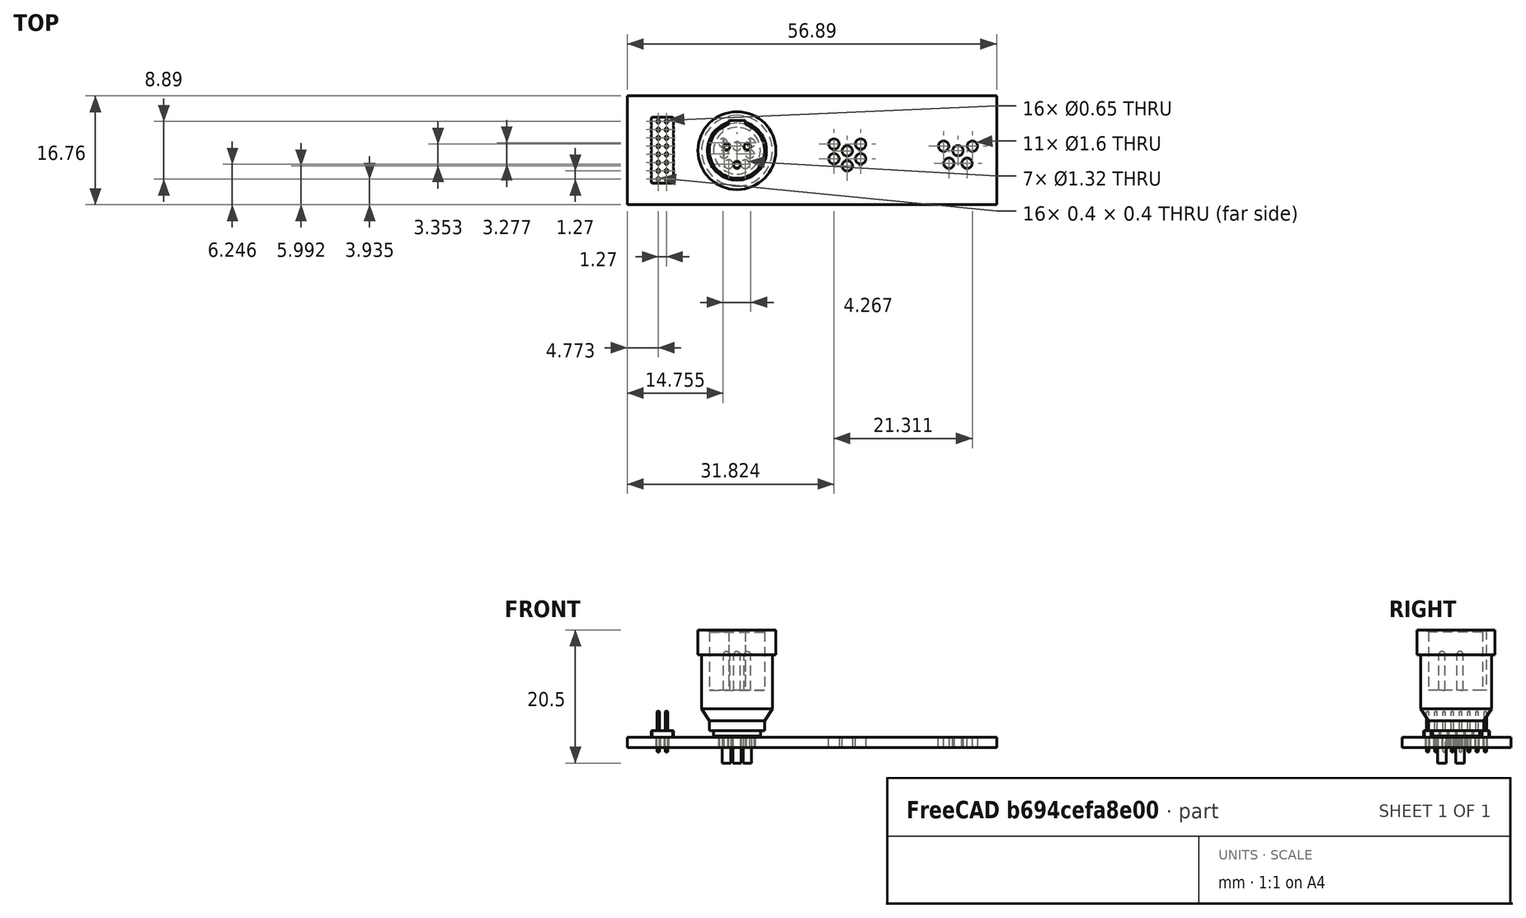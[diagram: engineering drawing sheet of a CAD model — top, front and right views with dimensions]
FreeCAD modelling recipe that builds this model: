
FCSTD DOCUMENT  (FreeCAD 1.0R39109 (Git))
Label: ConnectorInterfaceBoard
License: All rights reserved
LicenseURL: http://en.wikipedia.org/wiki/All_rights_reserved
objects: Part::Feature×9, App::Part×4, App::Link×2, PartDesign::CoordinateSystem×1, Sketcher::SketchObject×1
note: 12 computed .brp shape members not serialized (recipe doc carries the construction recipe); baked Part::Feature solids carry a one-line shape summary decoded from their .brp

FEATURE [PartDesign::CoordinateSystem] Local_CS_5996
  AttacherType = Attacher::AttachEngine3D
  MapMode = 2
FEATURE [Part::Feature] Pcb_5996
  shape: bbox 56.9 x 16.76 x 1.6 mm, 40 faces (baked)
FEATURE [Sketcher::SketchObject] PCB_Sketch_5996
  ArcFitTolerance = 1e-06
  FullyConstrained = false
  MakeInternals = false
  sketch-geometry (4):
    g0: LineSegment StartX=11.938 StartY=-11.938 StartZ=0 EndX=68.834 EndY=-11.938 EndZ=0
    g1: LineSegment StartX=68.834 StartY=-11.938 StartZ=0 EndX=68.834 EndY=-28.702 EndZ=0
    g2: LineSegment StartX=68.834 StartY=-28.702 StartZ=0 EndX=11.938 EndY=-28.702 EndZ=0
    g3: LineSegment StartX=11.938 StartY=-28.702 StartZ=0 EndX=11.938 EndY=-11.938 EndZ=0
  constraints (4):
    c: Coincident(g2,g3)
    c: Coincident(g0,g3)
    c: Coincident(g1,g2)
    c: Coincident(g0,g1)
FEATURE [Part::Feature] Shape  label="J4_PinHeader_2x08_P127mm_Vertical_934e7c050846"
  Placement = pos=(16.7132,-15.875,0) rot=(0,0,1;0rad)
  shape: bbox 3.4 x 10.16 x 6.3 mm, 340 faces (baked)
FEATURE [Part::Feature] Shape001  label="J1_RT3MP_764b897103e7"
  Placement = pos=(28.829,-20.3708,16.5) rot=(0,1,0;1.5708rad)
  shape: bbox 12 x 12 x 20.5 mm, 41 faces (baked)
FEATURE [App::Link] J1_RT3MP_764b897103e7_ln_  label="J3_RT3MP_9311650603bd"
  LinkPlacement = pos=(62.865,-20.3708,16.5) rot=(0.57735,0.57735,-0.57735;2.0944rad)
  LinkedObject = -> Shape001
  Placement = pos=(62.865,-20.3708,16.5) rot=(0.57735,0.57735,-0.57735;2.0944rad)
FEATURE [App::Link] J1_RT3MP_764b897103e7_ln_001  label="J2_RT3MP_923871eb31ec"
  LinkPlacement = pos=(45.8216,-20.3962,16.5) rot=(0,1,0;1.5708rad)
  LinkedObject = -> Shape001
  Placement = pos=(45.8216,-20.3962,16.5) rot=(0,1,0;1.5708rad)
FEATURE [App::Part] Top_5996
  Group = -> [Shape,Shape001,J1_RT3MP_764b897103e7_ln_,J1_RT3MP_764b897103e7_ln_001]
  Origin = -> Origin003
FEATURE [App::Part] Step_Models_5996
  Group = -> [Top_5996]
  Origin = -> Origin002
FEATURE [Part::Feature] pads_area001  label="topPads_5996"
  Placement = pos=(0,0,0.02) rot=(0,0,1;0rad)
  shape: bbox 52.14 x 13.81 x 2e-07 mm, 53 faces, 0 solids (baked)
FEATURE [Part::Feature] Shape003  label="topTracks_5996"
  Placement = pos=(0,0,0.01) rot=(0,0,1;0rad)
  shape: bbox 46.46 x 15.71 x 2e-07 mm, 15 faces, 0 solids (baked)
FEATURE [Part::Feature] zones_area001  label="topZones_5996"
  Placement = pos=(0,0,0.01) rot=(0,0,1;0rad)
  shape: bbox 56.8 x 16.66 x 2e-07 mm, 9 faces, 0 solids (baked)
FEATURE [Part::Feature] pads_area003  label="botPads_5996"
  Placement = pos=(0,0,-1.62) rot=(0,0,1;0rad)
  shape: bbox 52.14 x 13.81 x 2e-07 mm, 53 faces, 0 solids (baked)
FEATURE [Part::Feature] Shape005  label="botTracks_5996"
  Placement = pos=(0,0,-1.61) rot=(0,0,1;0rad)
  shape: bbox 53.24 x 14.74 x 2e-07 mm, 12 faces, 0 solids (baked)
FEATURE [Part::Feature] zones_area003  label="botZones_5996"
  Placement = pos=(0,0,-1.61) rot=(0,0,1;0rad)
  shape: bbox 56.8 x 16.66 x 2e-07 mm, 1 faces, 0 solids (baked)
FEATURE [App::Part] Board_Geoms_5996
  Group = -> [Pcb_5996,PCB_Sketch_5996,pads_area001,Shape003,zones_area001,pads_area003,Shape005,zones_area003]
  Origin = -> Origin
FEATURE [App::Part] Board_5996  label="ConnectorInterfaceBoard"
  Group = -> [Local_CS_5996,Board_Geoms_5996,Step_Models_5996]
  Origin = -> Origin001
